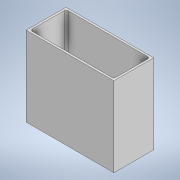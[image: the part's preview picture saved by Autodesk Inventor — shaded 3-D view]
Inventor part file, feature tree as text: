
AUTODESK INVENTOR PART (.ipt)
format: ipt  version: 2020 (Build 240168000, 168)  size: 110,592 bytes
history: native  units: mm
features: extrude x2, sketch x2
ambient origin geometry x8: Origin, YZ Plane, XZ Plane, XY Plane, X Axis, Y Axis, Z Axis, Center Point
bodies: Solid1 (feature_tree)
feature tree (4):
  extrude  "Extrusion1"  Depth=100.0mm
  extrude  "Extrusion2"  Depth=5.0mm
  sketch  "Sketch1"  dims[d0=220.0mm d1=100.0mm]
  sketch  "Sketch2"  dims[d2=200.0mm d3=0.0mm d4=5.0mm d5=5.0mm d6=5.0mm d7=5.0mm d8=5.0mm d9=195.0mm d10=0.0mm]
